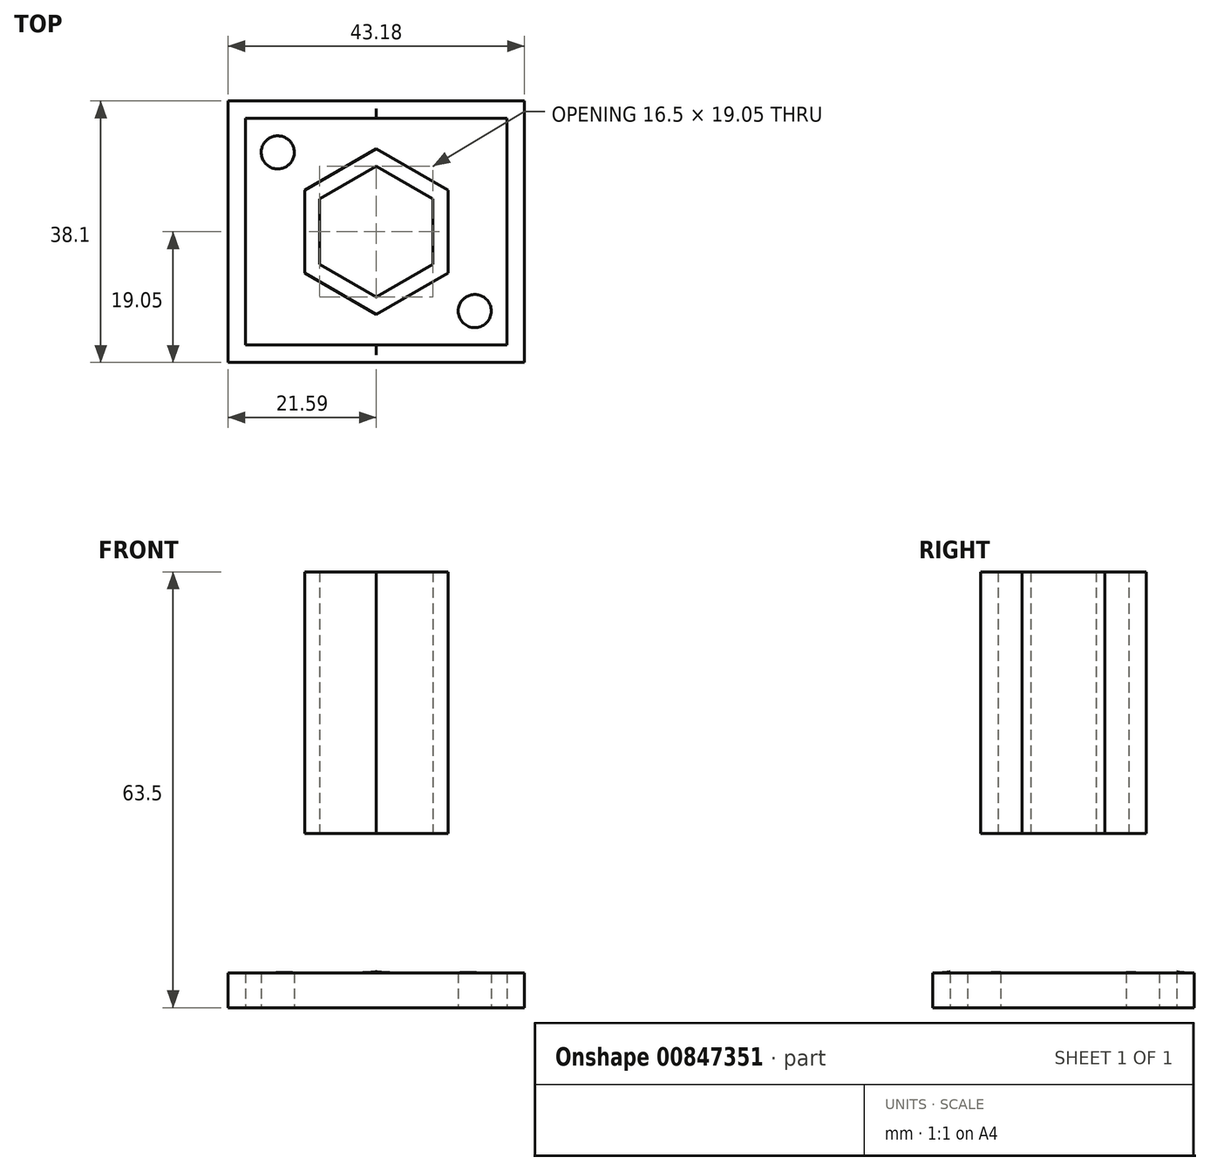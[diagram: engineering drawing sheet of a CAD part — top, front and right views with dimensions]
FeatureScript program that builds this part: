
annotation { "Feature Type Name" : "Feature", "Feature Type Description" : "" }
export const myFeature = defineFeature(function(context is Context, id is Id, definition is map)
    precondition{}
    {
        {
            var Q0;
            Q0=qCreatedBy(makeId("Front.planeOp"),FACE);
            var sketch = newSketch(context, id + "F0", { "sketchPlane" : qUnion([Q0])});
            skLineSegment(sketch, "E0.bottom", {"start": v(-21.59, -11.25) * mm, "end": v(21.59, -11.25) * mm});
            skLineSegment(sketch, "E0.top", {"start": v(-21.59, -16.33) * mm, "end": v(21.59, -16.33) * mm});
            skLineSegment(sketch, "E0.left", {"start": v(-21.59, -11.25) * mm, "end": v(-21.59, -16.33) * mm});
            skLineSegment(sketch, "E0.right", {"start": v(21.59, -11.25) * mm, "end": v(21.59, -16.33) * mm});
            skPoint(sketch, "E0.middle", {"position": v(0, -13.79) * mm});
            skSolve(sketch);
        }
        {
            var Q0;
            Q0 = qSketchRegion(id + "F0", true);
            extrude(context, id + "F1", {"entities" : qUnion([Q0]), "endBound" : BoundingType.SYMMETRIC, "depth" : 38.1 * mm, "offsetDistance" : 25.4 * mm});
        }
        {
            var Q0;
            Q0=makeQuery(id+"F1.opExtrude","SWEPT_FACE",FACE,{"disambiguationData":[OSD([sQuery(id+"F0.wireOp",EDGE,"E0.bottom")])]});
            var sketch = newSketch(context, id + "F2", { "sketchPlane" : qUnion([Q0])});
            skCircle(sketch, "E1", {"center": v(0, 0) * mm, "radius": 12.07 * mm, "construction": true});
            skLineSegment(sketch, "E2.0", {"start": v(0, 12.07) * mm, "end": v(10.45, 6.03) * mm});
            skLineSegment(sketch, "E2.1", {"start": v(10.45, 6.03) * mm, "end": v(10.45, -6.03) * mm});
            skLineSegment(sketch, "E2.2", {"start": v(10.45, -6.03) * mm, "end": v(0, -12.07) * mm});
            skLineSegment(sketch, "E2.3", {"start": v(0, -12.06) * mm, "end": v(-10.45, -6.03) * mm});
            skLineSegment(sketch, "E2.4", {"start": v(-10.45, -6.03) * mm, "end": v(-10.45, 6.03) * mm});
            skLineSegment(sketch, "E2.5", {"start": v(-10.45, 6.03) * mm, "end": v(0, 12.07) * mm});
            skCircle(sketch, "E3", {"center": v(0, 0) * mm, "radius": 9.53 * mm, "construction": true});
            skLineSegment(sketch, "E4.0", {"start": v(0, 9.53) * mm, "end": v(8.25, 4.76) * mm});
            skLineSegment(sketch, "E4.1", {"start": v(8.25, 4.76) * mm, "end": v(8.25, -4.76) * mm});
            skLineSegment(sketch, "E4.2", {"start": v(8.25, -4.76) * mm, "end": v(0, -9.53) * mm});
            skLineSegment(sketch, "E4.3", {"start": v(0, -9.53) * mm, "end": v(-8.25, -4.76) * mm});
            skLineSegment(sketch, "E4.4", {"start": v(-8.25, -4.76) * mm, "end": v(-8.25, 4.76) * mm});
            skLineSegment(sketch, "E4.5", {"start": v(-8.25, 4.76) * mm, "end": v(0, 9.52) * mm});
            skSolve(sketch);
        }
        {
            var Q0;
            Q0 = qSketchRegion(id + "F2", true);
            extrude(context, id + "F3", {"entities" : qUnion([Q0]), "operationType" : NewBodyOperationType.ADD, "depth" : 58.42 * mm, "offsetDistance" : 25.4 * mm});
        }
        {
            var Q0;
            Q0=makeQuery(id+"F3.opExtrude","CAP_EDGE",EDGE,{"disambiguationData":[OSD([sQuery(id+"F2.wireOp",EDGE,"E2.1")])],"isStart":true});
            var Q1;
            Q1=makeQuery(id+"F3.opExtrude","CAP_EDGE",EDGE,{"disambiguationData":[OSD([sQuery(id+"F2.wireOp",EDGE,"E2.2")])],"isStart":true});
            var Q2;
            Q2=makeQuery(id+"F3.opExtrude","CAP_EDGE",EDGE,{"disambiguationData":[OSD([sQuery(id+"F2.wireOp",EDGE,"E2.3")])],"isStart":true});
            var Q3;
            Q3=makeQuery(id+"F3.opExtrude","CAP_EDGE",EDGE,{"disambiguationData":[OSD([sQuery(id+"F2.wireOp",EDGE,"E2.0")])],"isStart":true});
            var Q4;
            Q4=makeQuery(id+"F3.opExtrude","CAP_EDGE",EDGE,{"disambiguationData":[OSD([sQuery(id+"F2.wireOp",EDGE,"E2.5")])],"isStart":true});
            var Q5;
            Q5=makeQuery(id+"F3.opExtrude","CAP_EDGE",EDGE,{"disambiguationData":[OSD([sQuery(id+"F2.wireOp",EDGE,"E2.4")])],"isStart":true});
            fillet(context, id + "F4", {"entities" : qUnion([Q0, Q1, Q2, Q3, Q4, Q5]), "radius" : 5.08 * mm, "tangentPropagation" : true, "allowEdgeOverflow" : false});
        }
        {
            var Q0;
            Q0=makeQuery(id+"F1.opExtrude","SWEPT_FACE",FACE,{"disambiguationData":[OSD([sQuery(id+"F0.wireOp",EDGE,"E0.top")])]});
            var sketch = newSketch(context, id + "F5", { "sketchPlane" : qUnion([Q0])});
            skLineSegment(sketch, "E5.bottom", {"start": v(-19.05, 16.51) * mm, "end": v(19.05, 16.51) * mm});
            skLineSegment(sketch, "E5.top", {"start": v(-19.05, -16.51) * mm, "end": v(19.05, -16.51) * mm});
            skLineSegment(sketch, "E5.left", {"start": v(-19.05, 16.51) * mm, "end": v(-19.05, -16.51) * mm});
            skLineSegment(sketch, "E5.right", {"start": v(19.05, 16.51) * mm, "end": v(19.05, -16.51) * mm});
            skPoint(sketch, "E5.middle", {"position": v(0, 0) * mm});
            skCircle(sketch, "E6", {"center": v(-14.35, 11.56) * mm, "radius": 2.41 * mm});
            skCircle(sketch, "E7.MirrorC", {"center": v(14.35, 11.56) * mm, "radius": 2.41 * mm});
            skCircle(sketch, "E8.MirrorC", {"center": v(-14.35, -11.56) * mm, "radius": 2.41 * mm});
            skCircle(sketch, "E9.MirrorC", {"center": v(14.35, -11.56) * mm, "radius": 2.41 * mm});
            skSolve(sketch);
        }
        {
            var Q0;
            Q0=makeQuery(id+"F5.imprint","IMPRINT",FACE,{"disambiguationData":[TD([[makeQuery(id+"F5.imprint","IMPRINT",EDGE,{"derivedFrom":sQuery(id+"F5.wireOp",EDGE,"E6")}),1.0]])]});
            var Q1;
            Q1=makeQuery(id+"F5.imprint","IMPRINT",FACE,{"disambiguationData":[TD([[makeQuery(id+"F5.imprint","IMPRINT",EDGE,{"derivedFrom":sQuery(id+"F5.wireOp",EDGE,"E7.MirrorC")}),-1.0]])]});
            var Q2;
            Q2=makeQuery(id+"F5.imprint","IMPRINT",FACE,{"disambiguationData":[TD([[makeQuery(id+"F5.imprint","IMPRINT",EDGE,{"derivedFrom":sQuery(id+"F5.wireOp",EDGE,"E8.MirrorC")}),-1.0]])]});
            var Q3;
            Q3=makeQuery(id+"F5.imprint","IMPRINT",FACE,{"disambiguationData":[TD([[makeQuery(id+"F5.imprint","IMPRINT",EDGE,{"derivedFrom":sQuery(id+"F5.wireOp",EDGE,"E9.MirrorC")}),1.0]])]});
            extrude(context, id + "F6", {"entities" : qUnion([Q0, Q1, Q2, Q3]), "operationType" : NewBodyOperationType.REMOVE, "oppositeDirection" : true, "depth" : 25.4 * mm, "offsetDistance" : 25.4 * mm});
        }
    });
